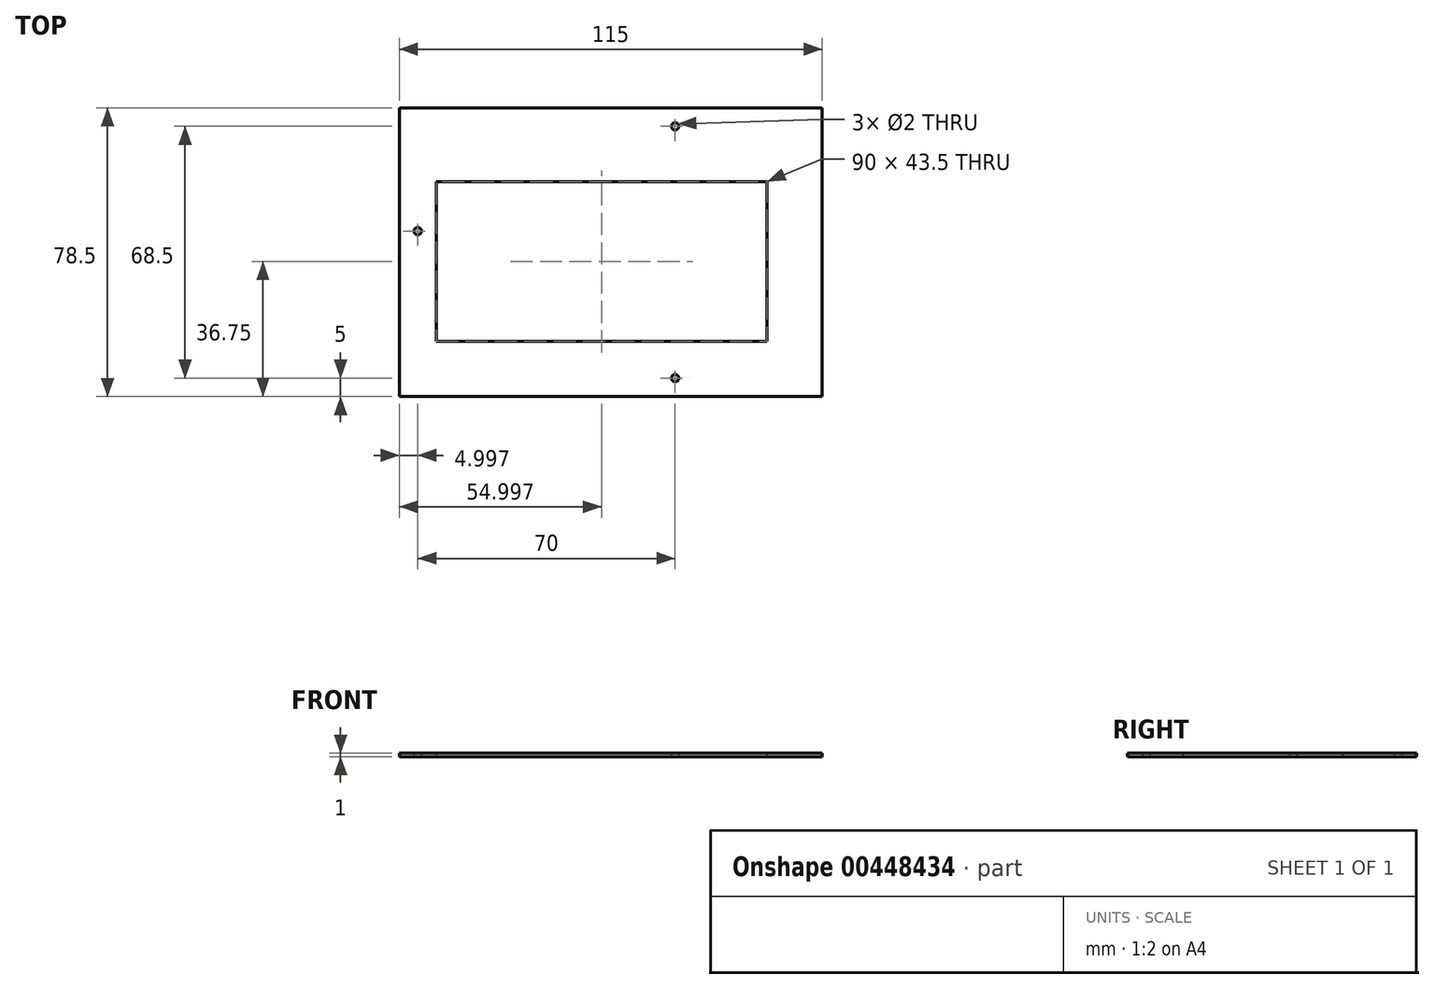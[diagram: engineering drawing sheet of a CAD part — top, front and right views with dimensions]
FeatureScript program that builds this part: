
annotation { "Feature Type Name" : "Feature", "Feature Type Description" : "" }
export const myFeature = defineFeature(function(context is Context, id is Id, definition is map)
    precondition{}
    {
        {
            var Q0;
            Q0=qCreatedBy(makeId("Top.planeOp"),FACE);
            var sketch = newSketch(context, id + "F0", { "sketchPlane" : qUnion([Q0])});
            skPoint(sketch, "E0", {"position": v(-52.56, 0) * mm});
            skPoint(sketch, "E1", {"position": v(17.44, 28.5) * mm});
            skPoint(sketch, "E2", {"position": v(17.44, -40) * mm});
            skLineSegment(sketch, "E3.bottom", {"start": v(-57.56, 33.5) * mm, "end": v(57.44, 33.5) * mm});
            skLineSegment(sketch, "E3.top", {"start": v(-57.56, -45) * mm, "end": v(57.44, -45) * mm});
            skLineSegment(sketch, "E3.left", {"start": v(-57.56, 33.5) * mm, "end": v(-57.56, -45) * mm});
            skLineSegment(sketch, "E3.right", {"start": v(57.44, 33.5) * mm, "end": v(57.44, -45) * mm});
            skLineSegment(sketch, "E4.bottom", {"start": v(-47.56, 13.5) * mm, "end": v(42.44, 13.5) * mm});
            skLineSegment(sketch, "E4.top", {"start": v(-47.56, -30) * mm, "end": v(42.44, -30) * mm});
            skLineSegment(sketch, "E4.left", {"start": v(-47.56, 13.5) * mm, "end": v(-47.56, -30) * mm});
            skLineSegment(sketch, "E4.right", {"start": v(42.44, 13.5) * mm, "end": v(42.44, -30) * mm});
            skSolve(sketch);
        }
        {
            var Q0;
            Q0=makeQuery(id+"F0.imprint","IMPRINT",FACE,{"disambiguationData":[TD([[makeQuery(id+"F0.imprint","IMPRINT",EDGE,{"derivedFrom":sQuery(id+"F0.wireOp",EDGE,"E3.bottom")}),-1.0]])]});
            extrude(context, id + "F1", {"entities" : qUnion([Q0]), "depth" : 1 * mm});
        }
        {
            var Q0;
            Q0=sQuery(id+"F0.wireOp",VERTEX,"E0");
            var Q1;
            Q1=sQuery(id+"F0.wireOp",VERTEX,"E1");
            var Q2;
            Q2=sQuery(id+"F0.wireOp",VERTEX,"E2");
            var Q3;
            Q3=makeQuery(id+"F1.opExtrude","SWEPT_BODY",BODY,{"disambiguationData":[OSD([sQuery(id+"F0.wireOp",EDGE,"E3.bottom"),sQuery(id+"F0.wireOp",EDGE,"E3.top"),sQuery(id+"F0.wireOp",EDGE,"E3.left"),sQuery(id+"F0.wireOp",EDGE,"E3.right"),sQuery(id+"F0.wireOp",EDGE,"E4.bottom"),sQuery(id+"F0.wireOp",EDGE,"E4.top"),sQuery(id+"F0.wireOp",EDGE,"E4.left"),sQuery(id+"F0.wireOp",EDGE,"E4.right")])]});
            hole(context, id + "F2", {"style" : HoleStyle.SIMPLE, "endStyle" : HoleEndStyle.THROUGH, "oppositeDirection" : true, "holeDiameter" : 2 * mm, "isTappedThrough" : true, "tappedDepth" : 12 * mm, "tapClearance" : 3, "locations" : qUnion([Q0, Q1, Q2]), "scope" : qUnion([Q3])});
        }
    });
